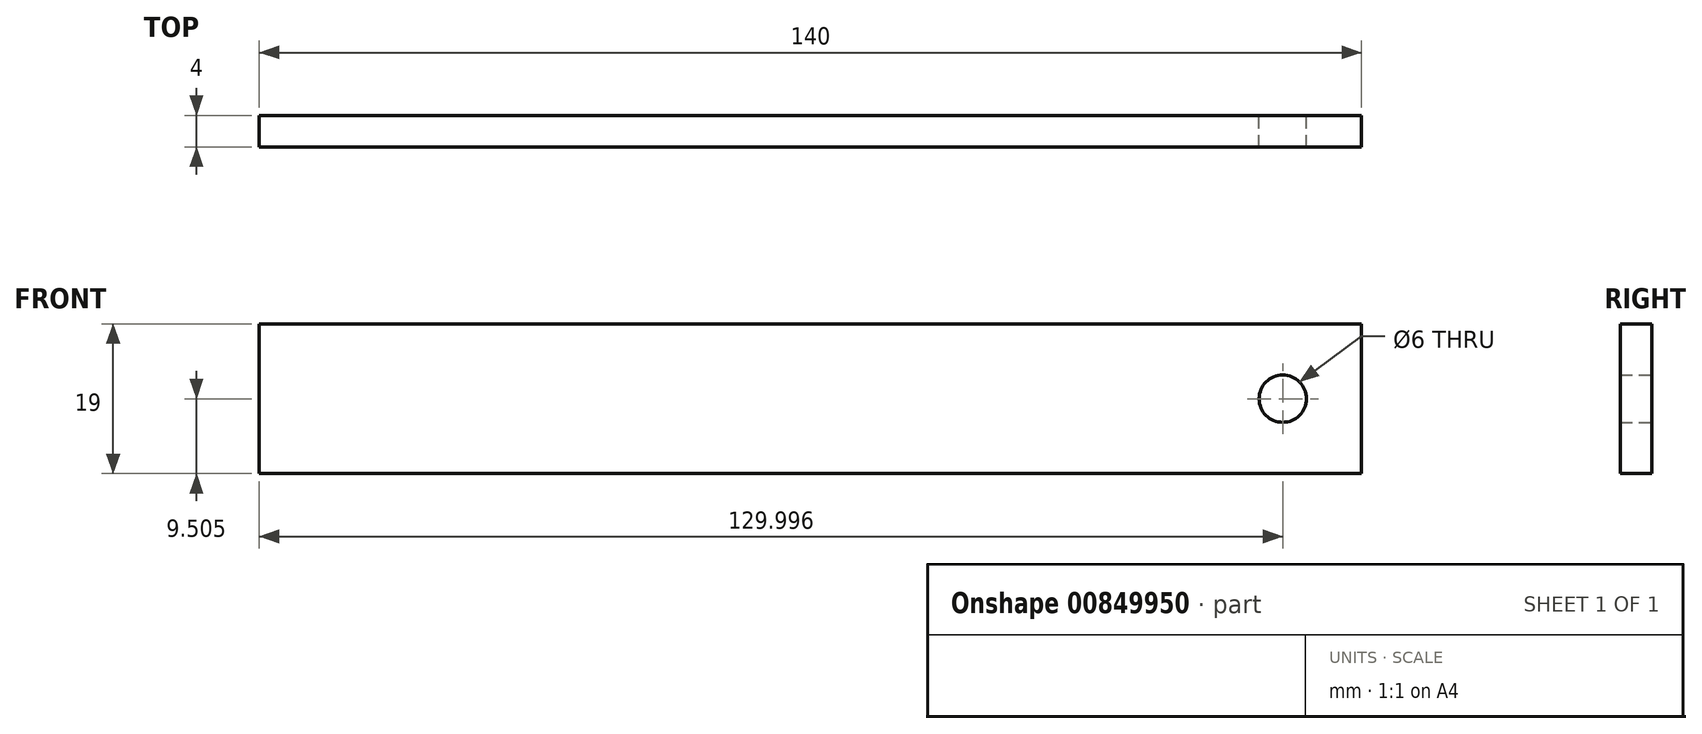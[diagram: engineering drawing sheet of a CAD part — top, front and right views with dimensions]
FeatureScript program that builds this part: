
annotation { "Feature Type Name" : "Feature", "Feature Type Description" : "" }
export const myFeature = defineFeature(function(context is Context, id is Id, definition is map)
    precondition{}
    {
        {
            var Q0;
            Q0=qCreatedBy(makeId("Front.planeOp"),FACE);
            var sketch = newSketch(context, id + "F0", { "sketchPlane" : qUnion([Q0])});
            skLineSegment(sketch, "E0.bottom", {"start": v(-2.93, -13.02) * mm, "end": v(137.07, -13.02) * mm});
            skLineSegment(sketch, "E0.top", {"start": v(-2.93, 5.98) * mm, "end": v(137.07, 5.98) * mm});
            skLineSegment(sketch, "E0.left", {"start": v(-2.93, -13.02) * mm, "end": v(-2.93, 5.98) * mm});
            skLineSegment(sketch, "E0.right", {"start": v(137.07, -13.02) * mm, "end": v(137.07, 5.98) * mm});
            skCircle(sketch, "E1", {"center": v(127.07, -3.52) * mm, "radius": 3 * mm});
            skPoint(sketch, "E1.centerSnap0", {"position": v(137.07, -3.52) * mm});
            skSolve(sketch);
        }
        {
            var Q0;
            Q0=makeQuery(id+"F0.imprint","IMPRINT",FACE,{"disambiguationData":[TD([[makeQuery(id+"F0.imprint","IMPRINT",EDGE,{"derivedFrom":sQuery(id+"F0.wireOp",EDGE,"E0.bottom")}),1.0]])]});
            extrude(context, id + "F1", {"entities" : qUnion([Q0]), "depth" : 4 * mm, "offsetDistance" : 25 * mm});
        }
    });
